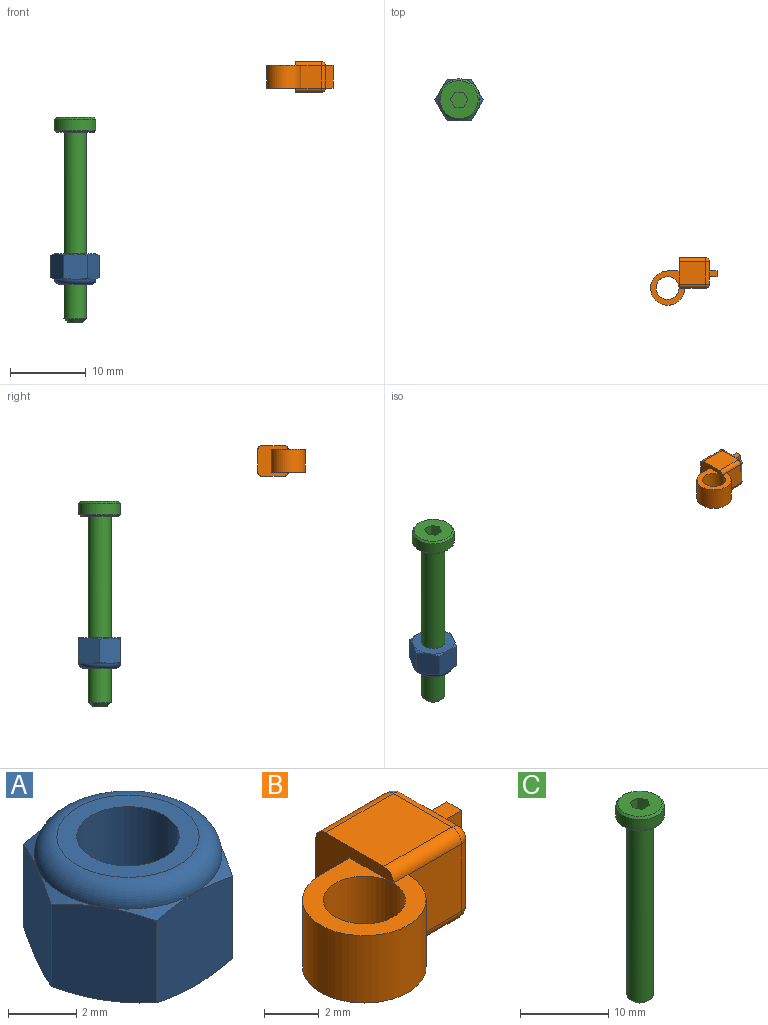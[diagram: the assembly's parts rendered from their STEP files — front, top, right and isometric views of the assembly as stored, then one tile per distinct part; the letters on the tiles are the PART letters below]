
ASSEMBLY  parts=3 mates=1
PART A: 22 faces, bbox 6.6x6.6x4.2 mm
  f0: plane 3.59x2.99mm, normal (-0.87,0.5,0), area 10.2mm2, adj f1,f5,f7,f9,f13,f14,f16,f21
  f1: plane 3.59x2.99mm, normal (-0.87,-0.5,0), area 10.2mm2, adj f0,f2,f7,f9,f10,f14,f20,f21
  f2: plane 3.6x3.42mm, normal (0,-1,0), area 10.2mm2, adj f1,f3,f7,f10,f11,f14,f19,f20
  f3: plane 3.59x2.99mm, normal (0.87,-0.5,0), area 10.2mm2, adj f2,f4,f7,f11,f12,f14,f18,f19
  f4: plane 3.59x2.99mm, normal (0.87,0.5,0), area 10.2mm2, adj f3,f5,f7,f12,f14,f15,f17,f18
  f5: plane 3.6x3.42mm, normal (0,1,0), area 10.2mm2, adj f0,f4,f7,f13,f14,f15,f16,f17
  f6: plane 4.17x4.17mm, normal (0,0,1), area 6.6mm2, adj f8,f14
  f7: plane 5.5x5.5mm, normal (0,0,-1), area 16.7mm2, adj f0,f1,f2,f3,f4,f5,f8,f16
  f8: cylinder r=1.5mm len=4mm, axis (0,0,1), area 37.7mm2, adj f6,f7
  f9: cone r=3.18mm half-angle=65deg, axis (0,0,-1), area 0.7mm2, adj f0,f1,f14
  f10: cone r=3.18mm half-angle=65deg, axis (0,0,-1), area 0.7mm2, adj f1,f2,f14
  f11: cone r=3.18mm half-angle=65deg, axis (0,0,-1), area 0.7mm2, adj f2,f3,f14
  f12: cone r=3.18mm half-angle=65deg, axis (0,0,-1), area 0.7mm2, adj f3,f4,f14
  f13: cone r=3.18mm half-angle=65deg, axis (0,0,-1), area 0.7mm2, adj f0,f5,f14
  f14: torus R=2.08mm, axis (0,0,-1), area 16.5mm2, adj f0,f1,f2,f3,f4,f5,f6,f9
  f15: cone r=3.18mm half-angle=65deg, axis (0,0,-1), area 0.7mm2, adj f4,f5,f14
  f16: cone r=2.75mm half-angle=65deg, axis (0,0,1), area 0.7mm2, adj f0,f5,f7
  f17: cone r=2.75mm half-angle=65deg, axis (0,0,1), area 0.7mm2, adj f4,f5,f7
  f18: cone r=2.75mm half-angle=65deg, axis (0,0,1), area 0.7mm2, adj f3,f4,f7
  f19: cone r=2.75mm half-angle=65deg, axis (0,0,1), area 0.7mm2, adj f2,f3,f7
  f20: cone r=2.75mm half-angle=65deg, axis (0,0,1), area 0.7mm2, adj f1,f2,f7
  f21: cone r=2.75mm half-angle=65deg, axis (0,0,1), area 0.7mm2, adj f0,f1,f7
PART B: 29 faces, bbox 8.8x6.3x4 mm
  f0: plane 3x1.25mm, normal (1,0,0), area 3.8mm2, adj f13,f18,f23,f24
  f1: cylinder r=2.25mm len=4.5mm, axis (0,0,-1), area 31.8mm2, adj f3,f4,f6,f16
  f2: cylinder r=1.5mm len=3mm, axis (0,0,-1), area 28.3mm2, adj f3,f4
  f3: plane 4.5x4.5mm, normal (0,0,1), area 8.2mm2, adj f1,f2,f5,f16,f22
  f4: plane 4.5x4.5mm, normal (0,0,-1), area 8.2mm2, adj f1,f2,f5,f16,f25
  f5: plane 4x4mm, normal (-1,0,0), area 9mm2, adj f3,f4,f8,f9,f10,f16,f17,f19
  f6: plane 3x2.75mm, normal (0,-1,0), area 8.2mm2, adj f1,f22,f25,f28
  f7: plane 3x1mm, normal (1,0,0), area 3mm2, adj f14,f23,f24,f28
  f8: plane 3.5x3mm, normal (0,1,0), area 10.5mm2, adj f5,f17,f18,f19
  f9: plane 3.5x3mm, normal (0,0,1), area 10.5mm2, adj f5,f17,f22,f23
  f10: plane 3.5x3mm, normal (0,0,-1), area 10.5mm2, adj f5,f19,f24,f25
  f11: plane 3x0.75mm, normal (1,0,0), area 2.2mm2, adj f12,f13,f14,f15
  f12: plane 1x0.75mm, normal (0,0,1), area 0.8mm2, adj f11,f13,f14,f23
  f13: plane 3x1mm, normal (0,1,0), area 3mm2, adj f0,f11,f12,f15
  f14: plane 3x1mm, normal (0,-1,0), area 3mm2, adj f7,f11,f12,f15
  f15: plane 1x0.75mm, normal (0,0,-1), area 0.8mm2, adj f11,f13,f14,f24
  f16: plane 3x1.5mm, normal (0,1,0), area 4.5mm2, adj f1,f3,f4,f5
  f17: cylinder r=0.5mm len=3.5mm, axis (1,0,0), area 2.7mm2, adj f5,f8,f9,f20
  f18: cylinder r=0.5mm len=3mm, axis (0,0,1), area 2.4mm2, adj f0,f8,f20,f21
  f19: cylinder r=0.5mm len=3.5mm, axis (-1,0,0), area 2.7mm2, adj f5,f8,f10,f21
  f20: sphere r=0.5mm, area 0.4mm2, adj f17,f18,f23
  f21: sphere r=0.5mm, area 0.4mm2, adj f18,f19,f24
  f22: cylinder r=0.5mm len=3.5mm, axis (-1,0,0), area 2.7mm2, adj f3,f5,f6,f9,f26
  f23: cylinder r=0.5mm len=3mm, axis (0,-1,0), area 2.4mm2, adj f0,f7,f9,f12,f20,f26
  f24: cylinder r=0.5mm len=3mm, axis (0,1,0), area 2.4mm2, adj f0,f7,f10,f15,f21,f27
  f25: cylinder r=0.5mm len=3.5mm, axis (1,0,0), area 2.7mm2, adj f4,f5,f6,f10,f27
  f26: sphere r=0.5mm, area 0.4mm2, adj f22,f23,f28
  f27: sphere r=0.5mm, area 0.4mm2, adj f24,f25,f28
  f28: cylinder r=0.5mm len=3mm, axis (0,0,-1), area 2.4mm2, adj f6,f7,f26,f27
PART C: 15 faces, bbox 5.5x5.5x27 mm
  f0: plane 5x5mm, normal (0,0,1), area 16.2mm2, adj f3,f4,f5,f6,f7,f8,f11
  f1: cylinder r=2.75mm len=5.5mm, axis (0,0,-1), area 25.9mm2, adj f10,f11
  f2: plane 5x5mm, normal (0,0,-1), area 12.6mm2, adj f10,f12
  f3: plane 1.5x1mm, normal (-0.87,-0.5,0), area 1.7mm2, adj f0,f4,f8,f9
  f4: plane 1.5x1.15mm, normal (0,-1,0), area 1.7mm2, adj f0,f3,f5,f9
  f5: plane 1.5x1mm, normal (0.87,-0.5,0), area 1.7mm2, adj f0,f4,f6,f9
  f6: plane 1.5x1mm, normal (0.87,0.5,0), area 1.7mm2, adj f0,f5,f7,f9
  f7: plane 1.5x1.15mm, normal (0,1,0), area 1.7mm2, adj f0,f6,f8,f9
  f8: plane 1.5x1mm, normal (-0.87,0.5,0), area 1.7mm2, adj f0,f3,f7,f9
  f9: plane 2.31x2mm, normal (0,0,1), area 3.5mm2, adj f3,f4,f5,f6,f7,f8
  f10: cone r=2.75mm half-angle=45deg, axis (0,0,1), area 5.8mm2, adj f1,f2
  f11: cone r=2.5mm half-angle=45deg, axis (0,0,-1), area 5.8mm2, adj f0,f1
  f12: cylinder r=1.5mm len=24.5mm, axis (0,0,1), area 230.9mm2, adj f2,f14
  f13: plane 2x2mm, normal (0,0,-1), area 3.1mm2, adj f14
  f14: cone r=1mm half-angle=45deg, axis (0,0,1), area 5.6mm2, adj f12,f13
PLACE A rot(axis=(1,0,0),180deg) t=(-50,0,-16)mm
PLACE B t=(-22.55,-24.82,5.81)mm
PLACE C at identity fixed
MATE fastened A.f8 <-> C.f1  axis (0,0,-1) through (-50,0,-16)mm
